# Revit family: IS_Strada_A6853_BIM_DE
name_source: partatom
category: Plumbing Fixtures
revit_build: Autodesk Revit MEP 2016 (Build: 20161004_0715(x64)
units: mm (PartAtom-declared; Revit-internal decimal feet)

## family parameters
Always vertical = No
Cut with Voids When Loaded = No
Part Type = Normal
Room Calculation Point = No
Round Connector Dimension = Use Diameter
Shared = No
Work Plane-Based = No

## types (1)
- A6853AA - STRADA build-in bath shower lever operated
    BIMobject category = Taps & Mixers
    BOSUseNativeGeometries = 1
    Brand url = http://www.idealstandard.co.uk
    EAN code = https://4015413332378
    Edition number = 1
    IFC Classification = Sanitary Terminal
    Installation instructions = http://www.idealstandard.de
    Manufacturer name = Ideal Standard
    Material main = Brass
    Model = A6853AA
    NBS Reference Code = 35-06-07
    NBS Reference Description = Bath Water Supply Fittings
    Nominal height = 0
    Nominal width = 0
    NominalDepth = 0 mm  [stored 0 ft]
    NominalHeight = 183 mm
    NominalLength = 87 mm
    NominalWidth = 157 mm  [stored 0.515092 ft]
    OmniClass Code = 23-31 11 00
    OmniClass Description = Faucets
    Product Guid = 9f302d2b-35ca-444d-a63c-427cb4e6e798
    Product SKU = A6853
    Product data url = https://bimobject.com
    Product family = STRADA
    Product group = Bath & Shower Mixer
    Product name = STRADA build-in bath shower lever operated
    Product url = http://www.idealstandard.de
    QR code = http://bimobject.com
    Size = 183 x 87 x 157mm
    Technical description = http://www.idealstandard.de
    Uniclass 1.4 Code = L8212
    Uniclass 1.4 Description = Fittings
    Uniclass 2.0 Code = PR-35-06-07
    Uniclass 2.0 Description = Bath Water Supply Fittings
    Uniclass 2015 Code = Pr_40_20_87_07
    Uniclass 2015 Name = Bath manual water supply sets
    Weight Net (Kg) = 1.68

note: [stored X ft] marks values corroborated as IEEE doubles in the binary element streams (Revit-internal decimal feet)

## geometry (parser evidence)
native form markers: Blend x4, Sweep x1
no freeform markers — native parametric forms only
